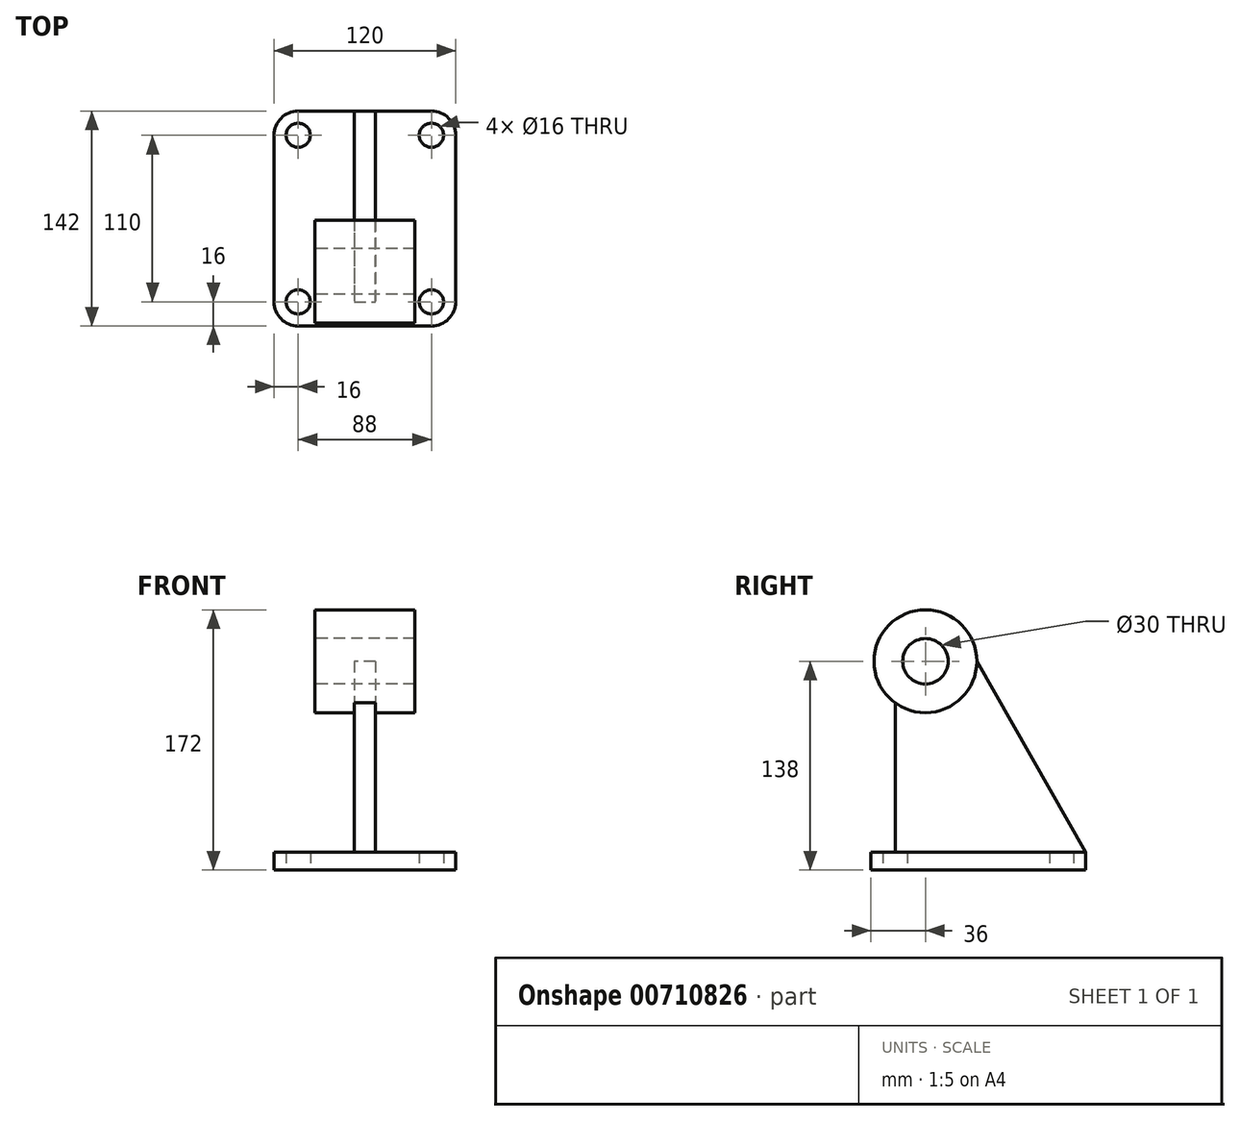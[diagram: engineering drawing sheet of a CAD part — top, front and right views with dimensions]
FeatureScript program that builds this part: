
annotation { "Feature Type Name" : "Feature", "Feature Type Description" : "" }
export const myFeature = defineFeature(function(context is Context, id is Id, definition is map)
    precondition{}
    {
        {
            var Q0;
            Q0=qCreatedBy(makeId("Top.planeOp"),FACE);
            var sketch = newSketch(context, id + "F0", { "sketchPlane" : qUnion([Q0])});
            skLineSegment(sketch, "E0.top", {"start": v(-44, -82) * mm, "end": v(44, -82) * mm});
            skLineSegment(sketch, "E0.left", {"start": v(-60, 44) * mm, "end": v(-60, -66) * mm});
            skLineSegment(sketch, "E0.right", {"start": v(60, 44) * mm, "end": v(60, -66) * mm});
            skPoint(sketch, "E1.visualSharp", {"position": v(-60, 60) * mm});
            skArc(sketch, "E1.filletArc", {"start": v(-44, 60) * mm, "mid": v(-55.31, 55.31) * mm, "end": v(-60, 44) * mm});
            skPoint(sketch, "E2.visualSharp", {"position": v(60, 60) * mm});
            skArc(sketch, "E2.filletArc", {"start": v(60, 44) * mm, "mid": v(55.31, 55.31) * mm, "end": v(44, 60) * mm});
            skPoint(sketch, "E3.visualSharp", {"position": v(60, -82) * mm});
            skArc(sketch, "E3.filletArc", {"start": v(44, -82) * mm, "mid": v(55.31, -77.31) * mm, "end": v(60, -66) * mm});
            skPoint(sketch, "E4.visualSharp", {"position": v(-60, -82) * mm});
            skArc(sketch, "E4.filletArc", {"start": v(-60, -66) * mm, "mid": v(-55.31, -77.31) * mm, "end": v(-44, -82) * mm});
            skCircle(sketch, "E5", {"center": v(44, 44) * mm, "radius": 8 * mm});
            skCircle(sketch, "E6", {"center": v(44, -66) * mm, "radius": 8 * mm});
            skCircle(sketch, "E7", {"center": v(-44, -66) * mm, "radius": 8 * mm});
            skCircle(sketch, "E8", {"center": v(-44, 44) * mm, "radius": 8 * mm});
            skLineSegment(sketch, "E9.trimOffspring", {"start": v(0, 60) * mm, "end": v(44, 60) * mm});
            skLineSegment(sketch, "E10", {"start": v(-44, 60) * mm, "end": v(0, 60) * mm});
            skSolve(sketch);
        }
        {
            var Q0;
            Q0=makeQuery(id+"F0.imprint","IMPRINT",FACE,{"disambiguationData":[TD([[makeQuery(id+"F0.imprint","IMPRINT",EDGE,{"derivedFrom":sQuery(id+"F0.wireOp",EDGE,"E0.top")}),1.0]])]});
            extrude(context, id + "F1", {"entities" : qUnion([Q0]), "depth" : 12 * mm, "offsetDistance" : 25 * mm});
        }
        {
            var Q0;
            Q0=makeQuery(id+"F1.opExtrude","CAP_FACE",FACE,{"disambiguationData":[OSD([sQuery(id+"F0.wireOp",EDGE,"E0.top"),sQuery(id+"F0.wireOp",EDGE,"E0.left"),sQuery(id+"F0.wireOp",EDGE,"E0.right"),sQuery(id+"F0.wireOp",EDGE,"E1.filletArc"),sQuery(id+"F0.wireOp",EDGE,"E2.filletArc"),sQuery(id+"F0.wireOp",EDGE,"E3.filletArc"),sQuery(id+"F0.wireOp",EDGE,"E4.filletArc"),sQuery(id+"F0.wireOp",EDGE,"E5"),sQuery(id+"F0.wireOp",EDGE,"E6"),sQuery(id+"F0.wireOp",EDGE,"E7"),sQuery(id+"F0.wireOp",EDGE,"E8"),sQuery(id+"F0.wireOp",EDGE,"E9.trimOffspring"),sQuery(id+"F0.wireOp",EDGE,"E10")])],"isStart":false});
            var sketch = newSketch(context, id + "F2", { "sketchPlane" : qUnion([Q0])});
            skLineSegment(sketch, "E11", {"start": v(0, 60) * mm, "end": v(7, 60) * mm});
            skLineSegment(sketch, "E12", {"start": v(0, 60) * mm, "end": v(-7, 60) * mm});
            skLineSegment(sketch, "E13", {"start": v(-7, 60) * mm, "end": v(-7, -66) * mm});
            skLineSegment(sketch, "E14", {"start": v(-7, -66) * mm, "end": v(7, -66) * mm});
            skLineSegment(sketch, "E15", {"start": v(7, -66) * mm, "end": v(7, 60) * mm});
            skSolve(sketch);
        }
        {
            var Q0;
            Q0=makeQuery(id+"F2.imprint","IMPRINT",FACE,{"disambiguationData":[TD([[makeQuery(id+"F2.imprint","IMPRINT",EDGE,{"derivedFrom":sQuery(id+"F2.wireOp",EDGE,"E11")}),-1.0]])]});
            extrude(context, id + "F3", {"entities" : qUnion([Q0]), "operationType" : NewBodyOperationType.ADD, "depth" : 126 * mm, "offsetDistance" : 25 * mm});
        }
        {
            var Q0;
            Q0=makeQuery(id+"F3.opExtrude","SWEPT_FACE",FACE,{"disambiguationData":[OSD([sQuery(id+"F2.wireOp",EDGE,"E13")])]});
            var sketch = newSketch(context, id + "F4", { "sketchPlane" : qUnion([Q0])});
            skLineSegment(sketch, "E16", {"start": v(66, 30.24) * mm, "end": v(46, 30.24) * mm});
            skLineSegment(sketch, "E17", {"start": v(11.13, 12) * mm, "end": v(11.13, 104) * mm});
            skCircle(sketch, "E18", {"center": v(46, 138) * mm, "radius": 34 * mm});
            skPoint(sketch, "E19.start.orphan", {"position": v(46, 104) * mm});
            skSolve(sketch);
        }
        {
            var Q0;
            Q0=qSketchRegion(id+"F4",true);
            extrude(context, id + "F5", {"entities" : qUnion([Q0]), "operationType" : NewBodyOperationType.ADD, "depth" : 26 * mm, "offsetDistance" : 25 * mm});
        }
        {
            var Q0;
            Q0=qSketchRegion(id+"F4",true);
            extrude(context, id + "F6", {"entities" : qUnion([Q0]), "operationType" : NewBodyOperationType.ADD, "oppositeDirection" : true, "depth" : 40 * mm, "offsetDistance" : 25 * mm});
        }
        {
            var Q0;
            Q0=makeQuery(id+"F5.opExtrude","CAP_FACE",FACE,{"disambiguationData":[OSD([sQuery(id+"F4.wireOp",EDGE,"E18")])],"isStart":false});
            var sketch = newSketch(context, id + "F7", { "sketchPlane" : qUnion([Q0])});
            skCircle(sketch, "E20", {"center": v(46, 138) * mm, "radius": 15 * mm});
            skSolve(sketch);
        }
        {
            var Q0;
            Q0=makeQuery(id+"F7.imprint","IMPRINT",FACE,{"disambiguationData":[TD([[makeQuery(id+"F7.imprint","IMPRINT",EDGE,{"derivedFrom":sQuery(id+"F7.wireOp",EDGE,"E20")}),1.0]])]});
            extrude(context, id + "F8", {"entities" : qUnion([Q0]), "operationType" : NewBodyOperationType.REMOVE, "oppositeDirection" : true, "depth" : 66 * mm, "offsetDistance" : 25 * mm});
        }
        {
            var Q0;
            Q0=makeQuery(id+"F3.opExtrude","SWEPT_FACE",FACE,{"disambiguationData":[OSD([sQuery(id+"F2.wireOp",EDGE,"E13")])]});
            var sketch = newSketch(context, id + "F9", { "sketchPlane" : qUnion([Q0])});
            skLineSegment(sketch, "E21", {"start": v(12, 138) * mm, "end": v(-60, 12) * mm});
            skSolve(sketch);
        }
        {
            var Q0;
            Q0=makeQuery(id+"F9.imprint","IMPRINT",FACE,{"disambiguationData":[TD([[makeQuery(id+"F9.imprint","IMPRINT",EDGE,{"derivedFrom":sQuery(id+"F9.wireOp",EDGE,"E21")}),-1.0]])]});
            extrude(context, id + "F10", {"entities" : qUnion([Q0]), "operationType" : NewBodyOperationType.REMOVE, "oppositeDirection" : true, "depth" : 14 * mm, "offsetDistance" : 25 * mm});
        }
    });
